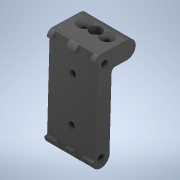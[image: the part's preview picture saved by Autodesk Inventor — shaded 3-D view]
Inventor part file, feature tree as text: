
AUTODESK INVENTOR PART (.ipt)
format: ipt  version: 2020.4 (Build 244396010, 396A)  size: 256,512 bytes
history: native  units: in
note: dims shown in document units (in); Inventor stores cm internally (conversion verified against a paired STEP export)
features: extrude x1, sketch x1
ambient origin geometry x8: Origin, YZ Plane, XZ Plane, XY Plane, X Axis, Y Axis, Z Axis, Center Point
bodies: Solid2 (feature_tree), Solid1 (feature_tree)
feature tree (2):
  extrude  "Extrusion1"  Depth=0.3937in
  sketch  "Sketch1"  dims[d0=0.126in d1=0.126in d2=0.3937in d3=0.0in]
